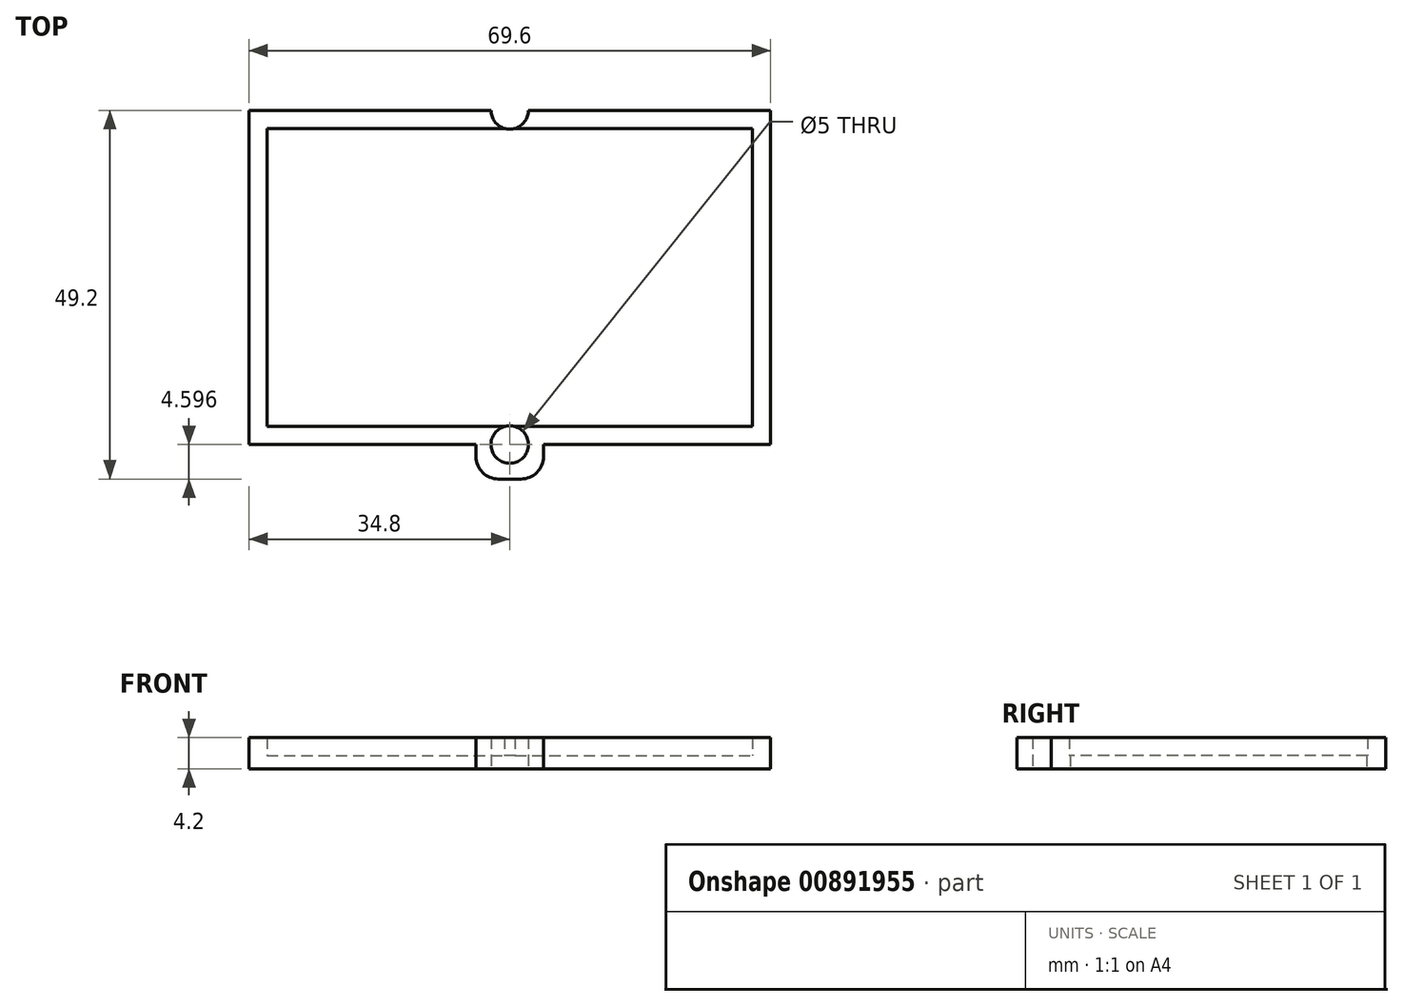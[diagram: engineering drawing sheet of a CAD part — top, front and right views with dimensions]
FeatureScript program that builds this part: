
annotation { "Feature Type Name" : "Feature", "Feature Type Description" : "" }
export const myFeature = defineFeature(function(context is Context, id is Id, definition is map)
    precondition{}
    {
        {
            var Q0;
            Q0=qCreatedBy(makeId("Top.planeOp"),FACE);
            var sketch = newSketch(context, id + "F0", { "sketchPlane" : qUnion([Q0])});
            skLineSegment(sketch, "E0.bottom", {"start": v(-30.3, -14.5) * mm, "end": v(29.7, -14.5) * mm});
            skLineSegment(sketch, "E0.top", {"start": v(-30.3, 20.5) * mm, "end": v(29.7, 20.5) * mm});
            skLineSegment(sketch, "E0.left", {"start": v(-30.3, -14.5) * mm, "end": v(-30.3, 20.5) * mm});
            skLineSegment(sketch, "E0.right", {"start": v(29.7, -14.5) * mm, "end": v(29.7, 20.5) * mm});
            skLineSegment(sketch, "E1.bottom", {"start": v(-32.7, 22.9) * mm, "end": v(32.1, 22.9) * mm});
            skLineSegment(sketch, "E1.top", {"start": v(-32.7, -16.9) * mm, "end": v(-4.8, -16.9) * mm});
            skLineSegment(sketch, "E1.left", {"start": v(-32.7, 22.9) * mm, "end": v(-32.7, -16.9) * mm});
            skLineSegment(sketch, "E1.right", {"start": v(32.1, 22.9) * mm, "end": v(32.1, -16.9) * mm});
            skLineSegment(sketch, "E2", {"start": v(-0.3, -16.9) * mm, "end": v(-0.3, 22.9) * mm, "construction": true});
            skCircle(sketch, "E3", {"center": v(-0.3, -19.3) * mm, "radius": 2.5 * mm});
            skLineSegment(sketch, "E4", {"start": v(-30.3, 3) * mm, "end": v(29.7, 3) * mm, "construction": true});
            skLineSegment(sketch, "E5", {"start": v(-4.8, -16.9) * mm, "end": v(-4.8, -20.9) * mm});
            skLineSegment(sketch, "E6", {"start": v(-1.8, -23.9) * mm, "end": v(1.2, -23.9) * mm});
            skLineSegment(sketch, "E7", {"start": v(4.2, -20.9) * mm, "end": v(4.2, -16.9) * mm});
            skPoint(sketch, "E8.visualSharp", {"position": v(-4.8, -23.9) * mm});
            skArc(sketch, "E8.filletArc", {"start": v(-4.8, -20.9) * mm, "mid": v(-3.92, -23.03) * mm, "end": v(-1.8, -23.9) * mm});
            skPoint(sketch, "E9.visualSharp", {"position": v(4.2, -23.9) * mm});
            skArc(sketch, "E9.filletArc", {"start": v(1.2, -23.9) * mm, "mid": v(3.32, -23.03) * mm, "end": v(4.2, -20.9) * mm});
            skLineSegment(sketch, "E10.0", {"start": v(-35.1, 25.3) * mm, "end": v(-2.8, 25.3) * mm});
            skLineSegment(sketch, "E10.1", {"start": v(-35.1, 25.3) * mm, "end": v(-35.1, -19.3) * mm});
            skLineSegment(sketch, "E10.2", {"start": v(-35.1, -19.3) * mm, "end": v(-4.8, -19.3) * mm});
            skLineSegment(sketch, "E10.3", {"start": v(34.5, 25.3) * mm, "end": v(34.5, -19.3) * mm});
            skPoint(sketch, "E11.orphan", {"position": v(-4.8, 22.9) * mm});
            skPoint(sketch, "E12.orphan", {"position": v(4.2, 22.9) * mm});
            skLineSegment(sketch, "E13.trimOffspring", {"start": v(2.2, 25.3) * mm, "end": v(34.5, 25.3) * mm});
            skLineSegment(sketch, "E14.trimOffspring", {"start": v(4.2, -19.3) * mm, "end": v(34.5, -19.3) * mm});
            skLineSegment(sketch, "E15.trimOffspring", {"start": v(4.2, -16.9) * mm, "end": v(32.1, -16.9) * mm});
            skLineSegment(sketch, "E16", {"start": v(-2.8, 25.3) * mm, "end": v(2.2, 25.3) * mm});
            skCircle(sketch, "E17.MirrorC", {"center": v(-0.3, 25.3) * mm, "radius": 2.5 * mm});
            skLineSegment(sketch, "E18.MirrorCS", {"start": v(-4.8, 22.9) * mm, "end": v(-4.8, 26.9) * mm});
            skArc(sketch, "E19.MirrorCS", {"start": v(-4.8, 26.9) * mm, "mid": v(-3.92, 29.02) * mm, "end": v(-1.8, 29.9) * mm});
            skLineSegment(sketch, "E20.MirrorCS", {"start": v(-1.8, 29.9) * mm, "end": v(1.2, 29.9) * mm});
            skArc(sketch, "E21.MirrorCS", {"start": v(1.2, 29.9) * mm, "mid": v(3.32, 29.02) * mm, "end": v(4.2, 26.9) * mm});
            skLineSegment(sketch, "E22.MirrorCS", {"start": v(4.2, 26.9) * mm, "end": v(4.2, 22.9) * mm});
            skLineSegment(sketch, "E23", {"start": v(-4.8, -16.9) * mm, "end": v(4.2, -16.9) * mm});
            skSolve(sketch);
        }
        {
            var Q0;
            {var subQ6=sQuery(id+"F0.wireOp",EDGE,"E1.top");Q0=makeQuery(id+"F0.imprint","IMPRINT",FACE,{"disambiguationData":[TD([[makeQuery(id+"F0.imprint","IMPRINT",EDGE,{"derivedFrom":subQ6}),-1.0]])]});}
            var Q1;
            {var subQ1=sQuery(id+"F0.wireOp",EDGE,"E1.right");Q1=makeQuery(id+"F0.imprint","IMPRINT",FACE,{"disambiguationData":[TD([[makeQuery(id+"F0.imprint","IMPRINT",EDGE,{"derivedFrom":subQ1}),1.0]])]});}
            var Q2;
            {var subQ0=sQuery(id+"F0.wireOp",EDGE,"E22.MirrorCS");var subQ1=sQuery(id+"F0.wireOp",EDGE,"E1.bottom");var subQ2=makeQuery(id+"F0.imprint","INTERSECT",VERTEX,{"derivedFrom":[subQ1,subQ0]});Q2=makeQuery(id+"F0.imprint","IMPRINT",FACE,{"disambiguationData":[TD([[makeQuery(id+"F0.imprint","IMPRINT",EDGE,{"disambiguationData":[TD([[subQ2,1.0]])],"derivedFrom":subQ1}),1.0]])]});}
            var Q3;
            {var subQ0=sQuery(id+"F0.wireOp",EDGE,"E18.MirrorCS");var subQ1=sQuery(id+"F0.wireOp",EDGE,"E1.bottom");var subQ2=makeQuery(id+"F0.imprint","INTERSECT",VERTEX,{"derivedFrom":[subQ1,subQ0]});Q3=makeQuery(id+"F0.imprint","IMPRINT",FACE,{"disambiguationData":[TD([[makeQuery(id+"F0.imprint","IMPRINT",EDGE,{"disambiguationData":[TD([[subQ2,-1.0]])],"derivedFrom":subQ1}),1.0]])]});}
            var Q4;
            {var subQ0=sQuery(id+"F0.wireOp",EDGE,"E19.MirrorCS");Q4=makeQuery(id+"F0.imprint","IMPRINT",FACE,{"disambiguationData":[TD([[makeQuery(id+"F0.imprint","IMPRINT",EDGE,{"derivedFrom":subQ0}),-1.0]])]});}
            var Q5;
            Q5=makeQuery(id+"F0.imprint","IMPRINT",FACE,{"disambiguationData":[TD([[makeQuery(id+"F0.imprint","IMPRINT",EDGE,{"derivedFrom":sQuery(id+"F0.wireOp",EDGE,"E6")}),1.0]])]});
            extrude(context, id + "F1", {"entities" : qUnion([Q0, Q1, Q2, Q3, Q4, Q5]), "depth" : 2.4 * mm, "offsetDistance" : 25 * mm});
        }
        {
            var Q0;
            {var subQ1=sQuery(id+"F0.wireOp",EDGE,"E1.right");Q0=makeQuery(id+"F0.imprint","IMPRINT",FACE,{"disambiguationData":[TD([[makeQuery(id+"F0.imprint","IMPRINT",EDGE,{"derivedFrom":subQ1}),1.0]])]});}
            var Q1;
            Q1=makeQuery(id+"F0.imprint","IMPRINT",FACE,{"disambiguationData":[TD([[makeQuery(id+"F0.imprint","IMPRINT",EDGE,{"derivedFrom":sQuery(id+"F0.wireOp",EDGE,"E0.bottom")}),-1.0]])]});
            var Q2;
            Q2=makeQuery(id+"F0.imprint","IMPRINT",FACE,{"disambiguationData":[TD([[makeQuery(id+"F0.imprint","IMPRINT",EDGE,{"derivedFrom":sQuery(id+"F0.wireOp",EDGE,"E0.bottom")}),1.0]])]});
            var Q3;
            {var subQ6=sQuery(id+"F0.wireOp",EDGE,"E1.top");Q3=makeQuery(id+"F0.imprint","IMPRINT",FACE,{"disambiguationData":[TD([[makeQuery(id+"F0.imprint","IMPRINT",EDGE,{"derivedFrom":subQ6}),-1.0]])]});}
            var Q4;
            Q4=makeQuery(id+"F0.imprint","IMPRINT",FACE,{"disambiguationData":[TD([[makeQuery(id+"F0.imprint","IMPRINT",EDGE,{"derivedFrom":sQuery(id+"F0.wireOp",EDGE,"E6")}),1.0]])]});
            var Q5;
            {var subQ0=sQuery(id+"F0.wireOp",EDGE,"E19.MirrorCS");Q5=makeQuery(id+"F0.imprint","IMPRINT",FACE,{"disambiguationData":[TD([[makeQuery(id+"F0.imprint","IMPRINT",EDGE,{"derivedFrom":subQ0}),-1.0]])]});}
            var Q6;
            {var subQ0=sQuery(id+"F0.wireOp",EDGE,"E22.MirrorCS");var subQ1=sQuery(id+"F0.wireOp",EDGE,"E1.bottom");var subQ2=makeQuery(id+"F0.imprint","INTERSECT",VERTEX,{"derivedFrom":[subQ1,subQ0]});Q6=makeQuery(id+"F0.imprint","IMPRINT",FACE,{"disambiguationData":[TD([[makeQuery(id+"F0.imprint","IMPRINT",EDGE,{"disambiguationData":[TD([[subQ2,1.0]])],"derivedFrom":subQ1}),1.0]])]});}
            var Q7;
            {var subQ0=sQuery(id+"F0.wireOp",EDGE,"E18.MirrorCS");var subQ1=sQuery(id+"F0.wireOp",EDGE,"E1.bottom");var subQ2=makeQuery(id+"F0.imprint","INTERSECT",VERTEX,{"derivedFrom":[subQ1,subQ0]});Q7=makeQuery(id+"F0.imprint","IMPRINT",FACE,{"disambiguationData":[TD([[makeQuery(id+"F0.imprint","IMPRINT",EDGE,{"disambiguationData":[TD([[subQ2,-1.0]])],"derivedFrom":subQ1}),1.0]])]});}
            extrude(context, id + "F2", {"entities" : qUnion([Q0, Q1, Q2, Q3, Q4, Q5, Q6, Q7]), "operationType" : NewBodyOperationType.ADD, "oppositeDirection" : true, "depth" : 1.8 * mm, "offsetDistance" : 25 * mm});
        }
    });
